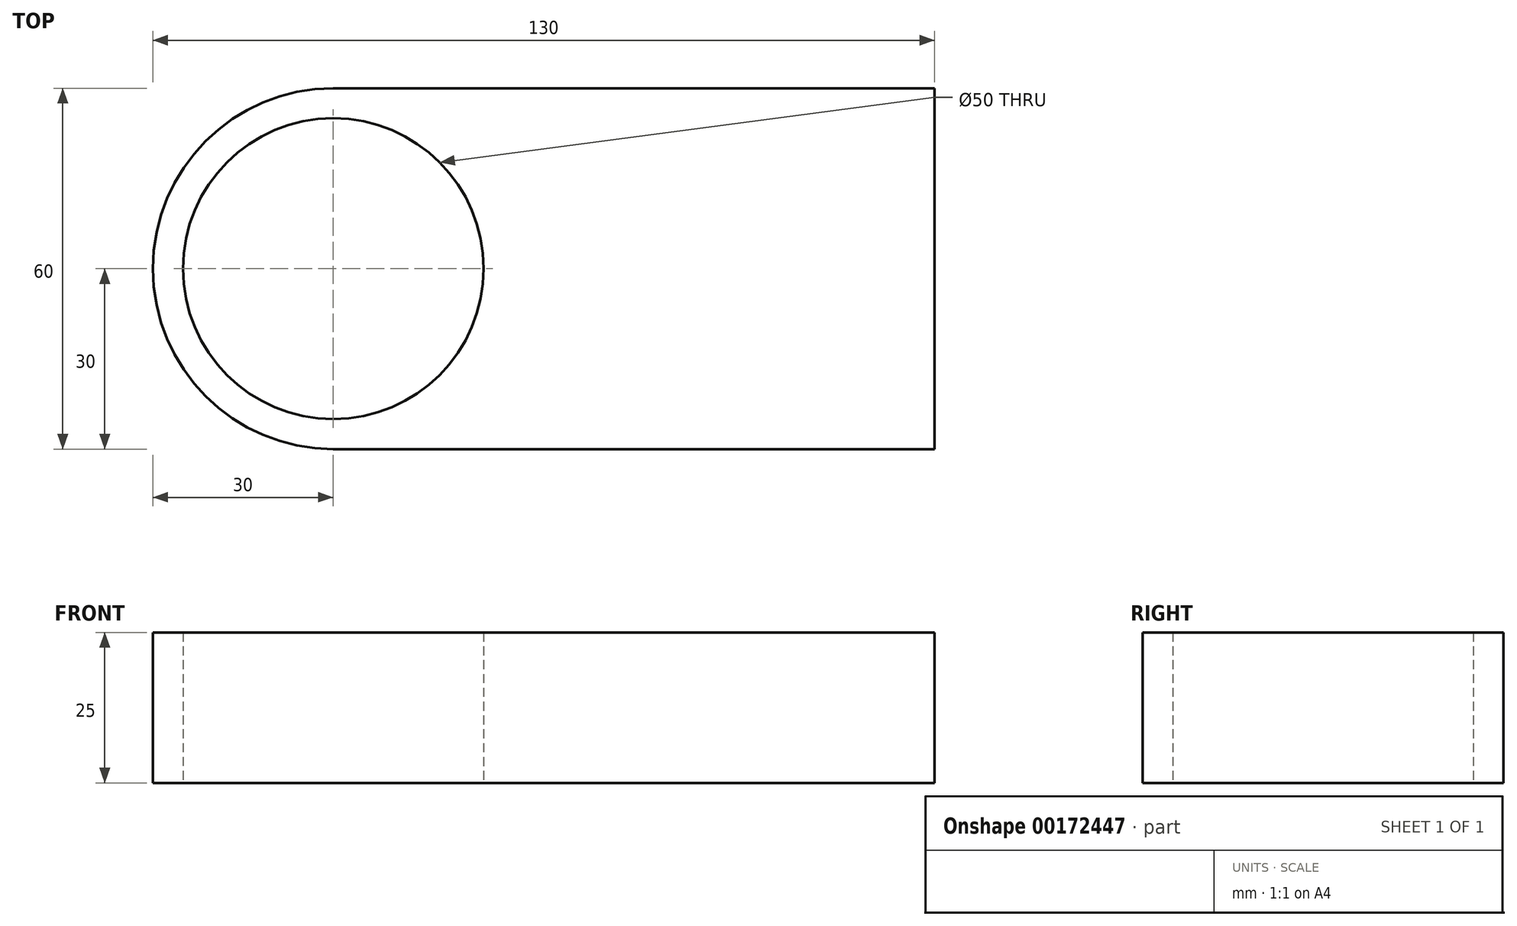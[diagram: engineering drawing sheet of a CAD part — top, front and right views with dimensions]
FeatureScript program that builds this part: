
annotation { "Feature Type Name" : "Feature", "Feature Type Description" : "" }
export const myFeature = defineFeature(function(context is Context, id is Id, definition is map)
    precondition{}
    {
        {
            var Q0;
            Q0=qCreatedBy(makeId("Top.planeOp"),FACE);
            var sketch = newSketch(context, id + "F0", { "sketchPlane" : qUnion([Q0])});
            skLineSegment(sketch, "E0.bottom", {"start": v(50, -30) * mm, "end": v(-50, -30) * mm});
            skLineSegment(sketch, "E0.top", {"start": v(50, 30) * mm, "end": v(-50, 30) * mm});
            skLineSegment(sketch, "E0.left", {"start": v(50, -30) * mm, "end": v(50, 30) * mm});
            skLineSegment(sketch, "E0.right", {"start": v(-50, -30) * mm, "end": v(-50, 30) * mm});
            skPoint(sketch, "E0.middle", {"position": v(0, 0) * mm});
            skCircle(sketch, "E1", {"center": v(-50, 0) * mm, "radius": 30 * mm});
            skCircle(sketch, "E2", {"center": v(-50, 0) * mm, "radius": 25 * mm});
            skSolve(sketch);
        }
        {
            var Q0;
            Q0 = qSketchRegion(id + "F0", true);
            extrude(context, id + "F1", {"entities" : qUnion([Q0]), "depth" : 25 * mm});
        }
    });
